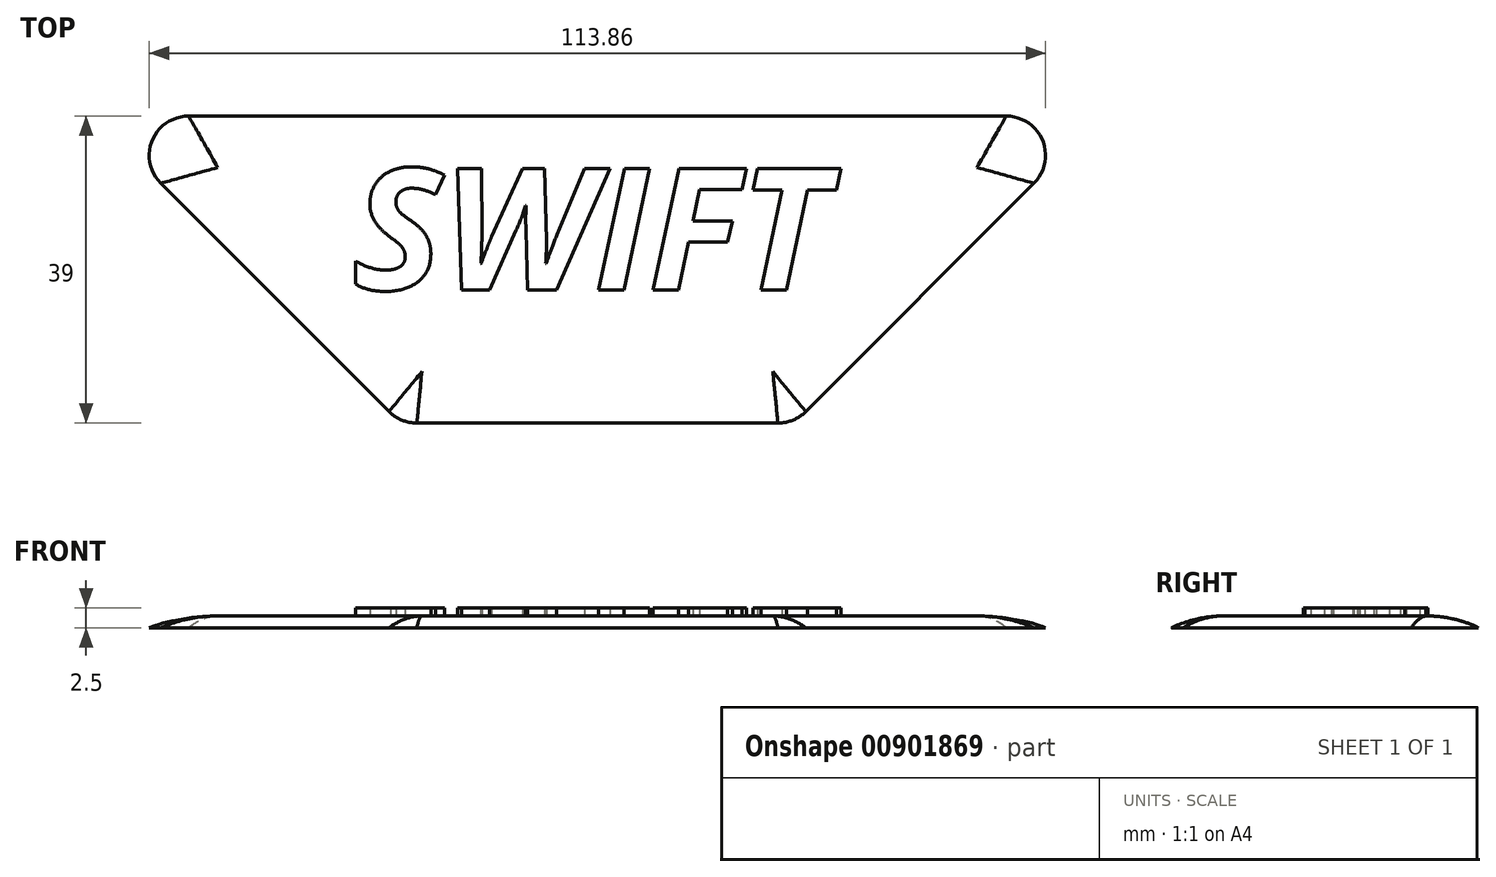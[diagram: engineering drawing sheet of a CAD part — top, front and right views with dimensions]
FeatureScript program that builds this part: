
annotation { "Feature Type Name" : "Feature", "Feature Type Description" : "" }
export const myFeature = defineFeature(function(context is Context, id is Id, definition is map)
    precondition{}
    {
        {
            var Q0;
            Q0=qCreatedBy(makeId("Top.planeOp"),FACE);
            var sketch = newSketch(context, id + "F0", { "sketchPlane" : qUnion([Q0])});
            skLineSegment(sketch, "E0", {"start": v(-53.14, 22.06) * mm, "end": v(50.72, 22.06) * mm});
            skLineSegment(sketch, "E1", {"start": v(54.26, 13.53) * mm, "end": v(25.26, -15.47) * mm});
            skLineSegment(sketch, "E2", {"start": v(21.72, -16.94) * mm, "end": v(-24.14, -16.94) * mm});
            skLineSegment(sketch, "E3", {"start": v(-27.67, -15.47) * mm, "end": v(-56.67, 13.53) * mm});
            skPoint(sketch, "E4.visualSharp", {"position": v(-65.2, 22.06) * mm});
            skArc(sketch, "E4.filletArc", {"start": v(-53.14, 22.06) * mm, "mid": v(-57.76, 18.98) * mm, "end": v(-56.67, 13.53) * mm});
            skPoint(sketch, "E5.visualSharp", {"position": v(62.8, 22.06) * mm});
            skArc(sketch, "E5.filletArc", {"start": v(54.26, 13.53) * mm, "mid": v(55.34, 18.98) * mm, "end": v(50.72, 22.06) * mm});
            skPoint(sketch, "E6.visualSharp", {"position": v(-26.2, -16.94) * mm});
            skArc(sketch, "E6.filletArc", {"start": v(-27.67, -15.47) * mm, "mid": v(-26.05, -16.56) * mm, "end": v(-24.14, -16.94) * mm});
            skPoint(sketch, "E7.visualSharp", {"position": v(23.8, -16.94) * mm});
            skArc(sketch, "E7.filletArc", {"start": v(21.72, -16.94) * mm, "mid": v(23.63, -16.56) * mm, "end": v(25.26, -15.47) * mm});
            skSolve(sketch);
        }
        {
            var Q0;
            Q0 = qSketchRegion(id + "F0", true);
            extrude(context, id + "F1", {"entities" : qUnion([Q0]), "depth" : 1.5 * mm, "offsetDistance" : 25 * mm});
        }
        {
            var Q0;
            Q0=makeQuery(id+"F1.opExtrude","CAP_FACE",FACE,{"disambiguationData":[OSD([sQuery(id+"F0.wireOp",EDGE,"E0"),sQuery(id+"F0.wireOp",EDGE,"E1"),sQuery(id+"F0.wireOp",EDGE,"E2"),sQuery(id+"F0.wireOp",EDGE,"E3"),sQuery(id+"F0.wireOp",EDGE,"E4.filletArc"),sQuery(id+"F0.wireOp",EDGE,"E5.filletArc"),sQuery(id+"F0.wireOp",EDGE,"E6.filletArc"),sQuery(id+"F0.wireOp",EDGE,"E7.filletArc")])],"isStart":false});
            fillet(context, id + "F2", {"entities" : qUnion([Q0]), "radius" : 15 * mm, "tangentPropagation" : true, "allowEdgeOverflow" : false});
        }
        {
            var Q0;
            Q0=makeQuery(id+"F1.opExtrude","CAP_FACE",FACE,{"disambiguationData":[OSD([sQuery(id+"F0.wireOp",EDGE,"E0"),sQuery(id+"F0.wireOp",EDGE,"E1"),sQuery(id+"F0.wireOp",EDGE,"E2"),sQuery(id+"F0.wireOp",EDGE,"E3"),sQuery(id+"F0.wireOp",EDGE,"E4.filletArc"),sQuery(id+"F0.wireOp",EDGE,"E5.filletArc"),sQuery(id+"F0.wireOp",EDGE,"E6.filletArc"),sQuery(id+"F0.wireOp",EDGE,"E7.filletArc")])],"isStart":false});
            var sketch = newSketch(context, id + "F3", { "sketchPlane" : qUnion([Q0])});
            skText(sketch, "E8", { "text": "SWIFT", "fontName": "OpenSans-BoldItalic.ttf"});
            const initialGuessF3  = {"E8": [-0.03233, 0, 1, 0, 0.01553]};
            skSetInitialGuess(sketch, initialGuessF3);
            skSolve(sketch);
        }
        {
            var Q0;
            Q0 = qSketchRegion(id + "F3", true);
            extrude(context, id + "F4", {"entities" : qUnion([Q0]), "operationType" : NewBodyOperationType.ADD, "depth" : 1 * mm, "offsetDistance" : 25 * mm});
        }
    });
